# Revit family: FabricDuct_RoundDiffuser_DuctSox_UFSox
name_source: partatom
category: Air Terminals
revit_build: Autodesk Revit 2017 (Build: 20160225_1515(x64)
units: mm (PartAtom-declared; Revit-internal decimal feet)

## family parameters
Always vertical = No
Cut with Voids When Loaded = No
OmniClass Number = 23.75.70.14
OmniClass Title = Air Ductwork
Part Type = Normal
Room Calculation Point = No
Round Connector Dimension = Use Radius
Shared = No
Work Plane-Based = No

## types (7) — shared parameters
Assembly Code = D3040100
Construction Details = https://www.ductsox.com
Description = DuctSox Sedona-Xm Round Endcap Diffuser
Green Building-LEED = https://www.arcat.com
Installation-Fabrication = http://www.ductsox.com
Keynote = 15810
Manufacturer = DuctSox
Manufacturer Fax = 563-588-5330
Manufacturer Website = http://www.ductsox.com
Model = Sedona-Xm
Product Data = https://www.arcat.com
Product Properties = http://www.ductsox.com
Revision = R1_03-2018
Sales Information = https://www.ductsox.com
Specification = http://www.arcat.com
Type Comments = Round Endcap Diffuser
URL = http://www.ductsox.com

## per-type parameters (varying)
| type | Fabric Color |
| Black | Fabric_Black |
| Silver | Fabric_Silver |
| White | Fabric_White |
| Green | Fabric_Green |
| Blue | Fabric_Blue |
| Red | Fabric_Red |
| Tan | Fabric_Tan |

## geometry (parser evidence)
native form markers: Sweep x4
no freeform markers — native parametric forms only
